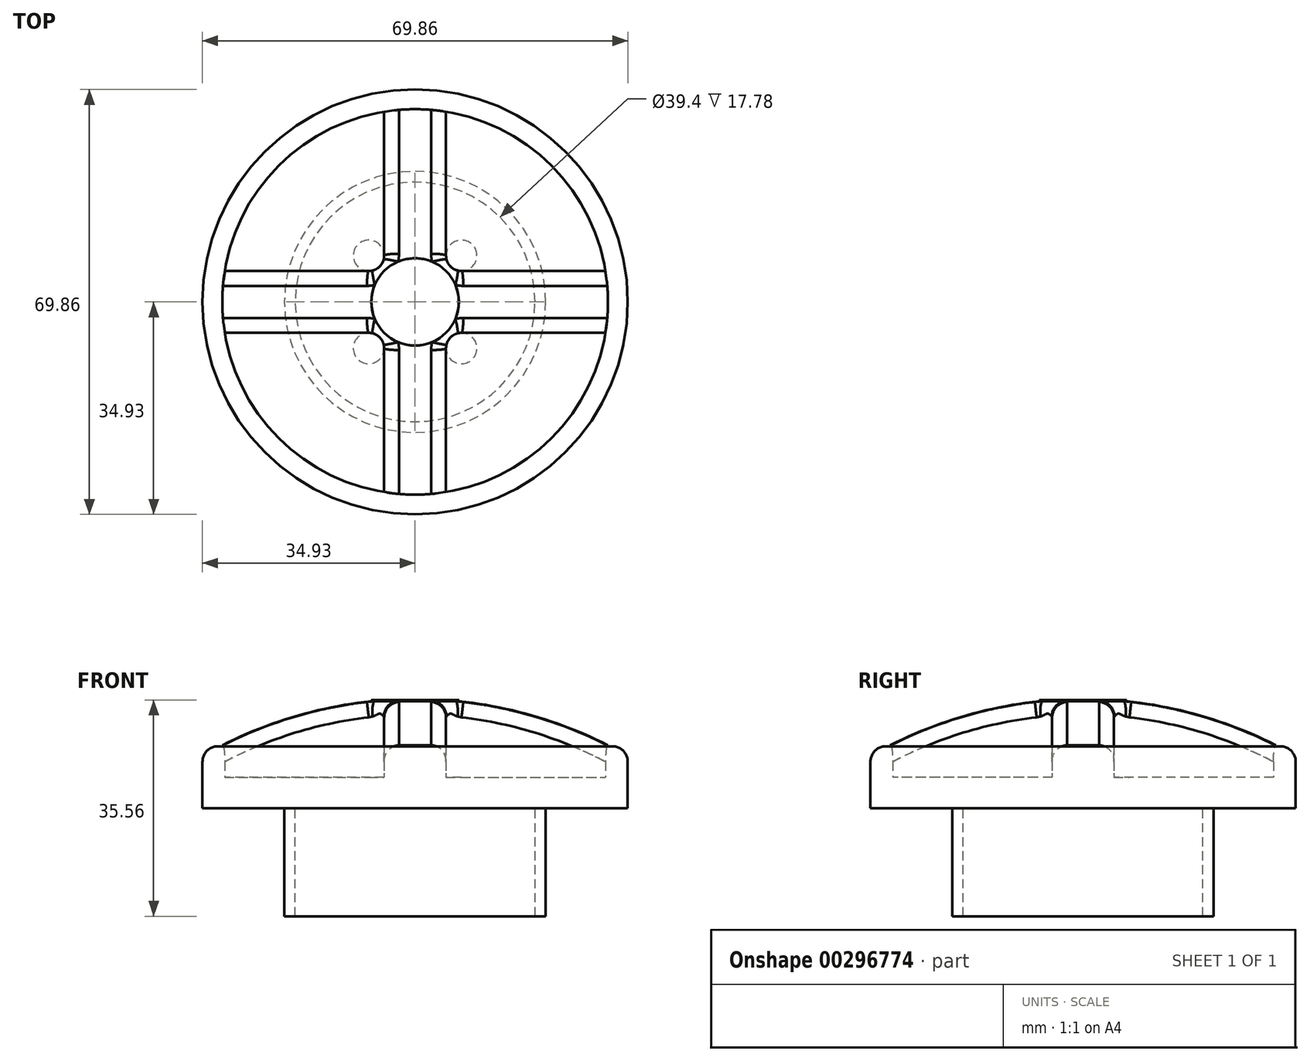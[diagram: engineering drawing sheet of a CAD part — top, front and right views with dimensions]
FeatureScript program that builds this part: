
annotation { "Feature Type Name" : "Feature", "Feature Type Description" : "" }
export const myFeature = defineFeature(function(context is Context, id is Id, definition is map)
    precondition{}
    {
        {
            var Q0;
            Q0=qCreatedBy(makeId("Top.planeOp"),FACE);
            var sketch = newSketch(context, id + "F0", { "sketchPlane" : qUnion([Q0])});
            skCircle(sketch, "E0", {"center": v(0, 0) * mm, "radius": 34.93 * mm});
            skSolve(sketch);
        }
        {
            var Q0;
            Q0=qCreatedBy(makeId("Right.planeOp"),FACE);
            var sketch = newSketch(context, id + "F1", { "sketchPlane" : qUnion([Q0])});
            skLineSegment(sketch, "E1", {"start": v(0, 0) * mm, "end": v(0, 52.54) * mm, "construction": true});
            skSolve(sketch);
        }
        {
            var Q0;
            Q0=makeQuery(id+"F0.imprint","IMPRINT",FACE,{"disambiguationData":[TD([[makeQuery(id+"F0.imprint","IMPRINT",EDGE,{"derivedFrom":sQuery(id+"F0.wireOp",EDGE,"E0")}),1.0]])]});
            extrude(context, id + "F2", {"entities" : qUnion([Q0]), "depth" : 5.08 * mm});
        }
        {
            var Q0;
            Q0=makeQuery(id+"F2.opExtrude","CAP_FACE",FACE,{"disambiguationData":[OSD([sQuery(id+"F0.wireOp",EDGE,"E0")])],"isStart":false});
            var sketch = newSketch(context, id + "F3", { "sketchPlane" : qUnion([Q0])});
            skCircle(sketch, "E2", {"center": v(0, 0) * mm, "radius": 31.68 * mm});
            skSolve(sketch);
        }
        {
            var Q0;
            Q0=makeQuery(id+"F3.imprint","IMPRINT",FACE,{"disambiguationData":[TD([[makeQuery(id+"F3.imprint","IMPRINT",EDGE,{"derivedFrom":sQuery(id+"F3.wireOp",EDGE,"E2")}),-1.0]])]});
            extrude(context, id + "F4", {"entities" : qUnion([Q0]), "operationType" : NewBodyOperationType.ADD, "depth" : 5.08 * mm});
        }
        {
            var Q0;
            Q0=makeQuery(id+"F2.opExtrude","CAP_FACE",FACE,{"disambiguationData":[OSD([sQuery(id+"F0.wireOp",EDGE,"E0")])],"isStart":false});
            var sketch = newSketch(context, id + "F5", { "sketchPlane" : qUnion([Q0])});
            skLineSegment(sketch, "E3.0", {"start": v(-5.08, 117.03) * mm, "end": v(-5.08, -9.92) * mm});
            skLineSegment(sketch, "E4.0", {"start": v(5.08, 114.4) * mm, "end": v(5.08, 9.92) * mm});
            skLineSegment(sketch, "E5.0", {"start": v(-118.66, -5.08) * mm, "end": v(-9.92, -5.08) * mm});
            skLineSegment(sketch, "E6.0", {"start": v(-114.32, 5.08) * mm, "end": v(9.92, 5.08) * mm});
            skLineSegment(sketch, "E7.trimOffspring", {"start": v(9.92, 5.08) * mm, "end": v(140.46, 5.08) * mm});
            skLineSegment(sketch, "E8.trimOffspring", {"start": v(5.08, 9.92) * mm, "end": v(5.08, -115.5) * mm});
            skLineSegment(sketch, "E9.trimOffspring", {"start": v(-9.92, -5.08) * mm, "end": v(128.43, -5.08) * mm});
            skLineSegment(sketch, "E10.trimOffspring", {"start": v(-5.08, -9.92) * mm, "end": v(-5.08, -114.38) * mm});
            skLineSegment(sketch, "E11", {"start": v(0, 0) * mm, "end": v(147.91, 0) * mm, "construction": true});
            skLineSegment(sketch, "E12", {"start": v(0, 0) * mm, "end": v(-126.43, 0) * mm, "construction": true});
            skSolve(sketch);
        }
        {
            var Q0;
            {var subQ0=sQuery(id+"F5.wireOp",EDGE,"qG3mWMhV-wTeE-VbPv-Plax-Hb3axC4Lr9U5");var subQ4=makeQuery(id+"F5.imprint","INTERSECT",VERTEX,{"derivedFrom":[sQuery(id+"F5.wireOp",EDGE,"E4.0"),subQ0]});Q0=makeQuery(id+"F5.imprint","IMPRINT",FACE,{"disambiguationData":[TD([[makeQuery(id+"F5.imprint","IMPRINT",EDGE,{"disambiguationData":[TD([[subQ4,1.0]])],"derivedFrom":subQ0}),1.0]])]});}
            var Q1;
            {var subQ0=sQuery(id+"F5.wireOp",EDGE,"qG3mWMhV-wTeE-VbPv-Plax-Hb3axC4Lr9U5");var subQ1=sQuery(id+"F5.wireOp",EDGE,"E5.0");var subQ2=makeQuery(id+"F5.imprint","INTERSECT",VERTEX,{"derivedFrom":[subQ1,subQ0]});Q1=makeQuery(id+"F5.imprint","IMPRINT",FACE,{"disambiguationData":[TD([[makeQuery(id+"F5.imprint","IMPRINT",EDGE,{"disambiguationData":[TD([[subQ2,1.0]])],"derivedFrom":subQ1}),1.0]])]});}
            var Q2;
            {var subQ0=sQuery(id+"F5.wireOp",EDGE,"qG3mWMhV-wTeE-VbPv-Plax-Hb3axC4Lr9U5");var subQ1=sQuery(id+"F5.wireOp",EDGE,"E3.0");var subQ2=makeQuery(id+"F5.imprint","INTERSECT",VERTEX,{"derivedFrom":[subQ1,subQ0]});Q2=makeQuery(id+"F5.imprint","IMPRINT",FACE,{"disambiguationData":[TD([[makeQuery(id+"F5.imprint","IMPRINT",EDGE,{"disambiguationData":[TD([[subQ2,1.0]])],"derivedFrom":subQ1}),1.0]])]});}
            var Q3;
            {var subQ0=sQuery(id+"F5.wireOp",EDGE,"E7.trimOffspring");var subQ1=sQuery(id+"F5.wireOp",EDGE,"qG3mWMhV-wTeE-VbPv-Plax-Hb3axC4Lr9U5");var subQ2=makeQuery(id+"F5.imprint","INTERSECT",VERTEX,{"derivedFrom":[subQ1,subQ0]});Q3=makeQuery(id+"F5.imprint","IMPRINT",FACE,{"disambiguationData":[TD([[makeQuery(id+"F5.imprint","IMPRINT",EDGE,{"disambiguationData":[TD([[subQ2,1.0]])],"derivedFrom":subQ1}),-1.0]])]});}
            var Q4;
            {var subQ0=sQuery(id+"F5.wireOp",EDGE,"E8.trimOffspring");var subQ1=sQuery(id+"F5.wireOp",EDGE,"qG3mWMhV-wTeE-VbPv-Plax-Hb3axC4Lr9U5");var subQ2=makeQuery(id+"F5.imprint","INTERSECT",VERTEX,{"derivedFrom":[subQ1,subQ0]});Q4=makeQuery(id+"F5.imprint","IMPRINT",FACE,{"disambiguationData":[TD([[makeQuery(id+"F5.imprint","IMPRINT",EDGE,{"disambiguationData":[TD([[subQ2,1.0]])],"derivedFrom":subQ1}),-1.0]])]});}
            var Q5;
            {var subQ3=sQuery(id+"F5.wireOp",EDGE,"E6.0");var subQ5=sQuery(id+"F5.wireOp",EDGE,"E3.0");var subQ6=makeQuery(id+"F5.imprint","INTERSECT",VERTEX,{"derivedFrom":[subQ5,subQ3]});Q5=makeQuery(id+"F5.imprint","IMPRINT",FACE,{"disambiguationData":[TD([[makeQuery(id+"F5.imprint","IMPRINT",EDGE,{"disambiguationData":[TD([[subQ6,1.0]])],"derivedFrom":subQ5}),1.0]])]});}
            var Q6;
            {var subQ5=sQuery(id+"F5.wireOp",EDGE,"E6.0");var subQ7=sQuery(id+"F5.wireOp",EDGE,"E7.trimOffspring");var subQ9=makeQuery(id+"F5.imprint","INTERSECT",VERTEX,{"derivedFrom":[subQ5,subQ7]});Q6=makeQuery(id+"F5.imprint","IMPRINT",FACE,{"disambiguationData":[TD([[makeQuery(id+"F5.imprint","IMPRINT",EDGE,{"disambiguationData":[TD([[subQ9,1.0]])],"derivedFrom":subQ5}),-1.0]])]});}
            var Q7;
            {var subQ0=sQuery(id+"F5.wireOp",EDGE,"E10.trimOffspring");var subQ1=sQuery(id+"F5.wireOp",EDGE,"E3.0");var subQ2=makeQuery(id+"F5.imprint","INTERSECT",VERTEX,{"derivedFrom":[subQ1,subQ0]});Q7=makeQuery(id+"F5.imprint","IMPRINT",FACE,{"disambiguationData":[TD([[makeQuery(id+"F5.imprint","IMPRINT",EDGE,{"disambiguationData":[TD([[subQ2,1.0]])],"derivedFrom":subQ1}),1.0]])]});}
            extrude(context, id + "F6", {"entities" : qUnion([Q0, Q1, Q2, Q3, Q4, Q5, Q6, Q7]), "operationType" : NewBodyOperationType.ADD, "depth" : 12.7 * mm});
        }
        {
            var Q0;
            Q0=makeQuery(id+"F6.opExtrude","SWEPT_FACE",FACE,{"disambiguationData":[OSD([sQuery(id+"F5.wireOp",EDGE,"E8.trimOffspring")])]});
            var sketch = newSketch(context, id + "F7", { "sketchPlane" : qUnion([Q0])});
            skArc(sketch, "E13", {"start": v(35.84, 8.04) * mm, "mid": v(-0.01, 17.78) * mm, "end": v(-35.8, 7.82) * mm});
            skLineSegment(sketch, "E14.0", {"start": v(31.27, 17.78) * mm, "end": v(5.08, 17.78) * mm});
            skLineSegment(sketch, "E15.0", {"start": v(31.27, 17.78) * mm, "end": v(31.27, 10.16) * mm});
            skSolve(sketch);
        }
        {
            var Q0;
            {var subQ0=sQuery(id+"F7.wireOp",EDGE,"E14.0");var subQ1=sQuery(id+"F7.wireOp",EDGE,"E13");var subQ2=makeQuery(id+"F7.imprint","INTERSECT",VERTEX,{"derivedFrom":[subQ1,subQ0]});Q0=makeQuery(id+"F7.imprint","IMPRINT",FACE,{"disambiguationData":[TD([[makeQuery(id+"F7.imprint","IMPRINT",EDGE,{"disambiguationData":[TD([[subQ2,1.0]])],"derivedFrom":subQ1}),-1.0]])]});}
            var Q1;
            Q1=sQuery(id+"F1.wireOp",EDGE,"E1");
            revolve(context, id + "F8", {"operationType" : NewBodyOperationType.REMOVE, "entities" : qUnion([Q0]), "axis" : qUnion([Q1]), "revolveType" : RevolveType.FULL, "oppositeDirection" : true});
        }
        {
            var Q0;
            Q0=makeQuery(id+"F2.opExtrude","CAP_FACE",FACE,{"disambiguationData":[OSD([sQuery(id+"F0.wireOp",EDGE,"E0")])],"isStart":true});
            var sketch = newSketch(context, id + "F9", { "sketchPlane" : qUnion([Q0])});
            skCircle(sketch, "E16", {"center": v(0, 0) * mm, "radius": 21.46 * mm});
            skCircle(sketch, "E17", {"center": v(0, 0) * mm, "radius": 19.7 * mm});
            skSolve(sketch);
        }
        {
            var Q0;
            Q0=makeQuery(id+"F9.imprint","IMPRINT",FACE,{"disambiguationData":[TD([[makeQuery(id+"F9.imprint","IMPRINT",EDGE,{"derivedFrom":sQuery(id+"F9.wireOp",EDGE,"E16")}),1.0]])]});
            extrude(context, id + "F10", {"entities" : qUnion([Q0]), "operationType" : NewBodyOperationType.ADD, "depth" : 17.78 * mm});
        }
        {
            var Q0;
            Q0=makeQuery(id+"F8.boolean.opBoolean","INTERSECT",EDGE,{"derivedFrom":[makeQuery(id+"F6.opExtrude","SWEPT_FACE",FACE,{"disambiguationData":[OSD([sQuery(id+"F5.wireOp",EDGE,"E9.trimOffspring")])]}),makeQuery(id+"F8.opRevolve","SWEPT_FACE",FACE,{"disambiguationData":[OSD([sQuery(id+"F7.wireOp",EDGE,"E13")])]})]});
            var Q1;
            Q1=makeQuery(id+"F8.boolean.opBoolean","INTERSECT",EDGE,{"derivedFrom":[makeQuery(id+"F6.opExtrude","SWEPT_FACE",FACE,{"disambiguationData":[OSD([sQuery(id+"F5.wireOp",EDGE,"E4.0"),sQuery(id+"F5.wireOp",EDGE,"E8.trimOffspring")])]}),makeQuery(id+"F8.opRevolve","SWEPT_FACE",FACE,{"disambiguationData":[OSD([sQuery(id+"F7.wireOp",EDGE,"E13")])]})]});
            var Q2;
            Q2=makeQuery(id+"F8.boolean.opBoolean","INTERSECT",EDGE,{"derivedFrom":[makeQuery(id+"F6.opExtrude","SWEPT_FACE",FACE,{"disambiguationData":[OSD([sQuery(id+"F5.wireOp",EDGE,"E6.0"),sQuery(id+"F5.wireOp",EDGE,"E7.trimOffspring")])]}),makeQuery(id+"F8.opRevolve","SWEPT_FACE",FACE,{"disambiguationData":[OSD([sQuery(id+"F7.wireOp",EDGE,"E13")])]})]});
            var Q3;
            Q3=makeQuery(id+"F6.opExtrude","SWEPT_EDGE",EDGE,{"disambiguationData":[OSD([sQuery(id+"F5.wireOp",EDGE,"E6.0"),sQuery(id+"F5.wireOp",EDGE,"E8.trimOffspring")])]});
            var Q4;
            Q4=makeQuery(id+"F6.opExtrude","SWEPT_EDGE",EDGE,{"disambiguationData":[OSD([sQuery(id+"F5.wireOp",EDGE,"E3.0"),sQuery(id+"F5.wireOp",EDGE,"E6.0")])]});
            var Q5;
            Q5=makeQuery(id+"F8.boolean.opBoolean","INTERSECT",EDGE,{"derivedFrom":[makeQuery(id+"F6.opExtrude","SWEPT_FACE",FACE,{"disambiguationData":[OSD([sQuery(id+"F5.wireOp",EDGE,"E6.0")])]}),makeQuery(id+"F8.opRevolve","SWEPT_FACE",FACE,{"disambiguationData":[OSD([sQuery(id+"F7.wireOp",EDGE,"E13")])]})]});
            var Q6;
            Q6=makeQuery(id+"F8.boolean.opBoolean","INTERSECT",EDGE,{"derivedFrom":[makeQuery(id+"F6.opExtrude","SWEPT_FACE",FACE,{"disambiguationData":[OSD([sQuery(id+"F5.wireOp",EDGE,"E3.0")])]}),makeQuery(id+"F8.opRevolve","SWEPT_FACE",FACE,{"disambiguationData":[OSD([sQuery(id+"F7.wireOp",EDGE,"E13")])]})]});
            var Q7;
            Q7=makeQuery(id+"F8.boolean.opBoolean","INTERSECT",EDGE,{"derivedFrom":[makeQuery(id+"F6.opExtrude","SWEPT_FACE",FACE,{"disambiguationData":[OSD([sQuery(id+"F5.wireOp",EDGE,"E5.0"),sQuery(id+"F5.wireOp",EDGE,"E9.trimOffspring")])]}),makeQuery(id+"F8.opRevolve","SWEPT_FACE",FACE,{"disambiguationData":[OSD([sQuery(id+"F7.wireOp",EDGE,"E13")])]})]});
            var Q8;
            Q8=makeQuery(id+"F6.opExtrude","SWEPT_EDGE",EDGE,{"disambiguationData":[OSD([sQuery(id+"F5.wireOp",EDGE,"E3.0"),sQuery(id+"F5.wireOp",EDGE,"E9.trimOffspring")])]});
            var Q9;
            Q9=makeQuery(id+"F8.boolean.opBoolean","INTERSECT",EDGE,{"derivedFrom":[makeQuery(id+"F6.opExtrude","SWEPT_FACE",FACE,{"disambiguationData":[OSD([sQuery(id+"F5.wireOp",EDGE,"E3.0"),sQuery(id+"F5.wireOp",EDGE,"E10.trimOffspring")])]}),makeQuery(id+"F8.opRevolve","SWEPT_FACE",FACE,{"disambiguationData":[OSD([sQuery(id+"F7.wireOp",EDGE,"E13")])]})]});
            var Q10;
            Q10=makeQuery(id+"F8.boolean.opBoolean","INTERSECT",EDGE,{"derivedFrom":[makeQuery(id+"F6.opExtrude","SWEPT_FACE",FACE,{"disambiguationData":[OSD([sQuery(id+"F5.wireOp",EDGE,"E8.trimOffspring")])]}),makeQuery(id+"F8.opRevolve","SWEPT_FACE",FACE,{"disambiguationData":[OSD([sQuery(id+"F7.wireOp",EDGE,"E13")])]})]});
            var Q11;
            Q11=makeQuery(id+"F6.opExtrude","SWEPT_EDGE",EDGE,{"disambiguationData":[OSD([sQuery(id+"F5.wireOp",EDGE,"E8.trimOffspring"),sQuery(id+"F5.wireOp",EDGE,"E9.trimOffspring")])]});
            var Q12;
            Q12=makeQuery(id+"F4.opExtrude","CAP_EDGE",EDGE,{"disambiguationData":[OSD([sQuery(id+"F0.wireOp",EDGE,"E0")])],"isStart":false});
            fillet(context, id + "F11", {"entities" : qUnion([Q0, Q1, Q2, Q3, Q4, Q5, Q6, Q7, Q8, Q9, Q10, Q11, Q12]), "radius" : 2.54 * mm, "tangentPropagation" : true, "allowEdgeOverflow" : false});
        }
    });
